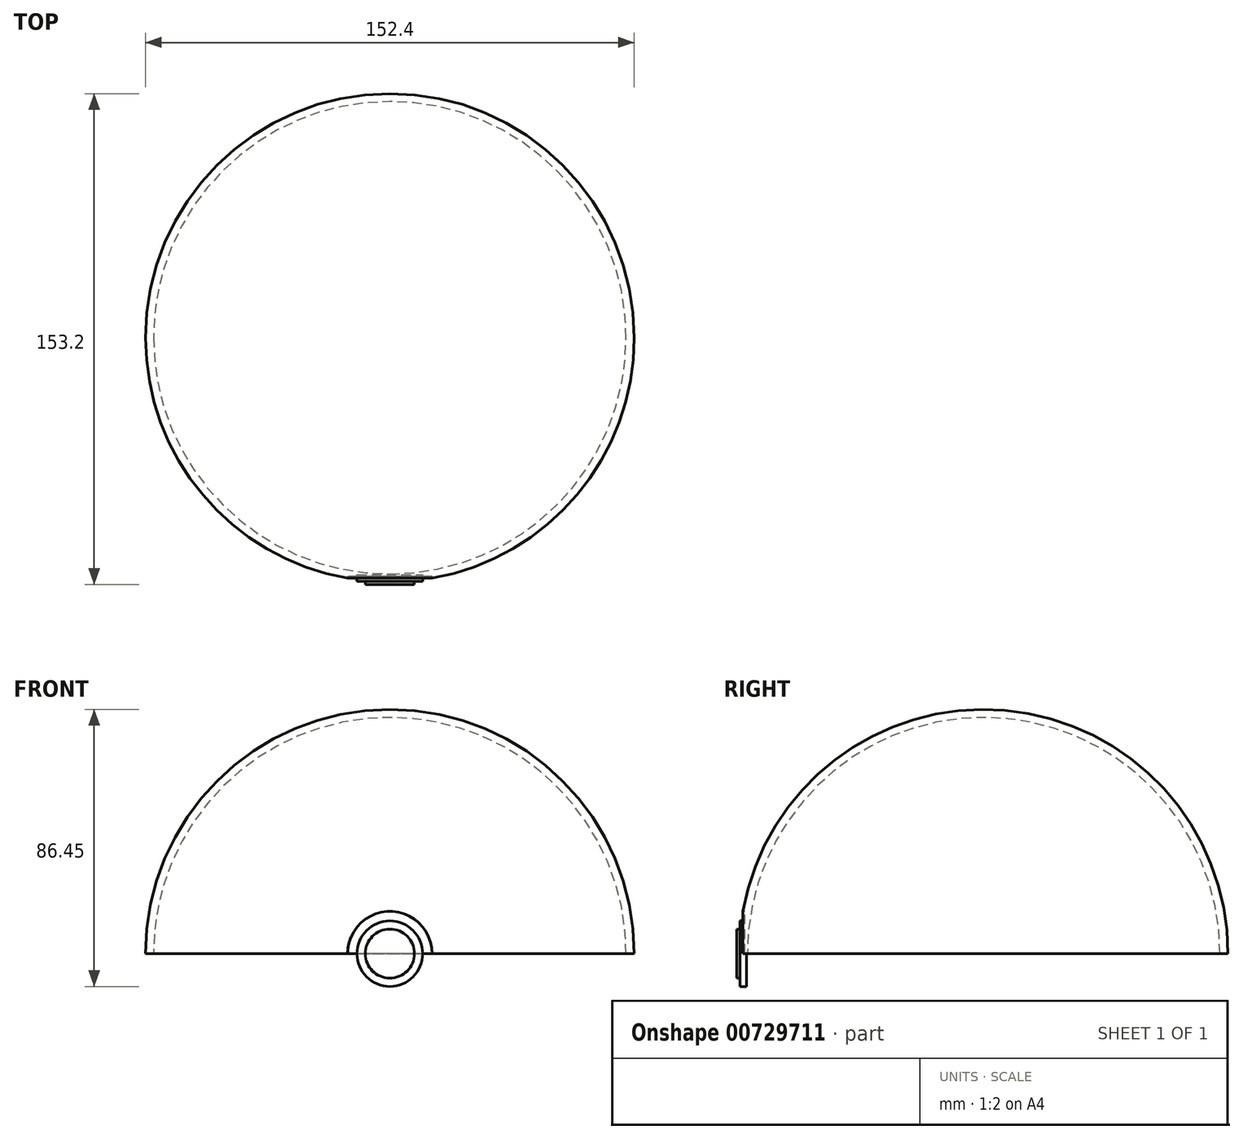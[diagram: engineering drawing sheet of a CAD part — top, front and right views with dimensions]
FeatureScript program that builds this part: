
annotation { "Feature Type Name" : "Feature", "Feature Type Description" : "" }
export const myFeature = defineFeature(function(context is Context, id is Id, definition is map)
    precondition{}
    {
        {
            var Q0;
            Q0=qCreatedBy(makeId("Front.planeOp"),FACE);
            var sketch = newSketch(context, id + "F0", { "sketchPlane" : qUnion([Q0])});
            skLineSegment(sketch, "E0", {"start": v(-76.2, 0) * mm, "end": v(76.2, 0) * mm});
            skArc(sketch, "E1", {"start": v(-76.2, 0) * mm, "mid": v(0, 76.2) * mm, "end": v(76.2, 0) * mm});
            skSolve(sketch);
        }
        {
            var Q0;
            Q0=makeQuery(id+"F0.imprint","IMPRINT",FACE,{"disambiguationData":[TD([[makeQuery(id+"F0.imprint","IMPRINT",EDGE,{"derivedFrom":sQuery(id+"F0.wireOp",EDGE,"E0")}),1.0]])]});
            var Q1;
            Q1=sQuery(id+"F0.wireOp",EDGE,"E0");
            revolve(context, id + "F1", {"surfaceOperationType" : NewSurfaceOperationType.NEW, "entities" : qUnion([Q0]), "axis" : qUnion([Q1]), "revolveType" : RevolveType.SYMMETRIC, "oppositeDirection" : true, "angle" : 180 * degree});
        }
        {
            var Q0;
            Q0=makeQuery(id+"F1.opRevolve","CAP_FACE",FACE,{"disambiguationData":[OSD([sQuery(id+"F0.wireOp",EDGE,"E0"),sQuery(id+"F0.wireOp",EDGE,"E1")])],"isStart":false});
            shell(context, id + "F2", {"entities" : qUnion([Q0]), "thickness" : 2.5 * mm});
        }
        {
            var Q0;
            Q0=qCreatedBy(makeId("Front.planeOp"),FACE);
            var sketch = newSketch(context, id + "F3", { "sketchPlane" : qUnion([Q0])});
            skCircle(sketch, "E2", {"center": v(0, 0) * mm, "radius": 10.25 * mm});
            skSolve(sketch);
        }
        {
            var Q0;
            Q0=makeQuery(id+"F3.imprint","IMPRINT",FACE,{"disambiguationData":[TD([[makeQuery(id+"F3.imprint","IMPRINT",EDGE,{"derivedFrom":sQuery(id+"F3.wireOp",EDGE,"E2")}),1.0]])]});
            extrude(context, id + "F4", {"entities" : qUnion([Q0]), "depth" : 74 * mm, "offsetDistance" : 25 * mm});
        }
        {
            var Q0;
            Q0=makeQuery(id+"F4.opExtrude","CAP_FACE",FACE,{"disambiguationData":[OSD([sQuery(id+"F3.wireOp",EDGE,"E2")])],"isStart":false});
            var sketch = newSketch(context, id + "F5", { "sketchPlane" : qUnion([Q0])});
            skCircle(sketch, "E3", {"center": v(0, 0) * mm, "radius": 10.27 * mm});
            skSolve(sketch);
        }
        {
            var Q0;
            Q0=makeQuery(id+"F5.imprint","IMPRINT",FACE,{"disambiguationData":[TD([[makeQuery(id+"F5.imprint","IMPRINT",EDGE,{"derivedFrom":makeQuery(id+"F4.opExtrude","CAP_EDGE",EDGE,{"disambiguationData":[OSD([sQuery(id+"F3.wireOp",EDGE,"E2")])],"isStart":false})}),1.0]])]});
            extrude(context, id + "F6", {"entities" : qUnion([Q0]), "depth" : 2 * mm, "offsetDistance" : 25 * mm});
        }
        {
            var Q0;
            Q0=makeQuery(id+"F6.opExtrude","CAP_FACE",FACE,{"disambiguationData":[OSD([sQuery(id+"F3.wireOp",EDGE,"E2")])],"isStart":false});
            var sketch = newSketch(context, id + "F7", { "sketchPlane" : qUnion([Q0])});
            skCircle(sketch, "E4", {"center": v(0, 0) * mm, "radius": 7.66 * mm});
            skSolve(sketch);
        }
        {
            var Q0;
            Q0=makeQuery(id+"F7.imprint","IMPRINT",FACE,{"disambiguationData":[TD([[makeQuery(id+"F7.imprint","IMPRINT",EDGE,{"derivedFrom":sQuery(id+"F7.wireOp",EDGE,"E4")}),1.0]])]});
            extrude(context, id + "F8", {"entities" : qUnion([Q0]), "operationType" : NewBodyOperationType.ADD, "depth" : 1 * mm, "offsetDistance" : 25 * mm});
        }
        {
            var Q0;
            Q0=makeQuery(id+"F6.opExtrude","CAP_FACE",FACE,{"disambiguationData":[OSD([sQuery(id+"F3.wireOp",EDGE,"E2")])],"isStart":false});
            var sketch = newSketch(context, id + "F9", { "sketchPlane" : qUnion([Q0])});
            skCircle(sketch, "E5", {"center": v(0, 0) * mm, "radius": 13.17 * mm});
            skSolve(sketch);
        }
        {
            var Q0;
            Q0=makeQuery(id+"F9.imprint","IMPRINT",FACE,{"disambiguationData":[TD([[makeQuery(id+"F9.imprint","IMPRINT",EDGE,{"derivedFrom":sQuery(id+"F9.wireOp",EDGE,"E5")}),1.0]])]});
            extrude(context, id + "F10", {"entities" : qUnion([Q0]), "operationType" : NewBodyOperationType.REMOVE, "oppositeDirection" : true, "depth" : 1.5 * mm, "offsetDistance" : 25 * mm});
        }
        {
            var Q0;
            Q0=makeQuery(id+"F4.opExtrude","SWEPT_BODY",BODY,{"disambiguationData":[OSD([sQuery(id+"F3.wireOp",EDGE,"E2")])]});
            deleteBodies(context, id + "F11", {"entities" : qUnion([Q0])});
        }
    });
